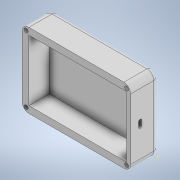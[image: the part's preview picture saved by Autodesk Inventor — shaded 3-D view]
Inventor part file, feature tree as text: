
AUTODESK INVENTOR PART (.ipt)
format: ipt  version: 2021 (Build 250183000, 183)  size: 245,760 bytes
history: native  units: mm
features: sketch x10, extrude x9, other x7, fillet x2, shell x1, projected_geometry x1
ambient origin geometry x8: Origin, YZ Plane, XZ Plane, XY Plane, X Axis, Y Axis, Z Axis, Center Point
bodies: Body1 (feature_tree)
feature tree (30):
  other  "솔리드1"
  extrude  "돌출1"  Depth=90.0mm
  fillet  "모깎기1"  Radius=55.0mm
  shell  "쉘1"  Thickness=20.0mm
  fillet  "모깎기2"  Radius=5.0mm
  extrude  "돌출2"  Depth=5.0mm
  other  "스레드1"
  other  "스레드2"
  other  "스레드3"
  other  "스레드4"
  extrude  "돌출3"  Depth=3.0mm
  extrude  "돌출4"  Depth=3.0mm
  extrude  "돌출5"  Depth=3.0mm
  other  "직접 편집1"
  extrude  "돌출6"  Depth=3.0mm
  sketch  "스케치8"
  extrude  "돌출7"  Depth=3.0mm
  extrude  "돌출8"  Depth=3.0mm
  extrude  "돌출9"  Depth=15.0mm TaperAngle=0.0deg
  sketch  "스케치1"
  sketch  "스케치2"
  sketch  "스케치3"
  sketch  "스케치4"
  projected_geometry  "투영된 루프1"
  sketch  "스케치6"
  sketch  "스케치7"
  sketch  "스케치9"
  sketch  "스케치10"
  sketch  "스케치11"
  other  "이동1"
